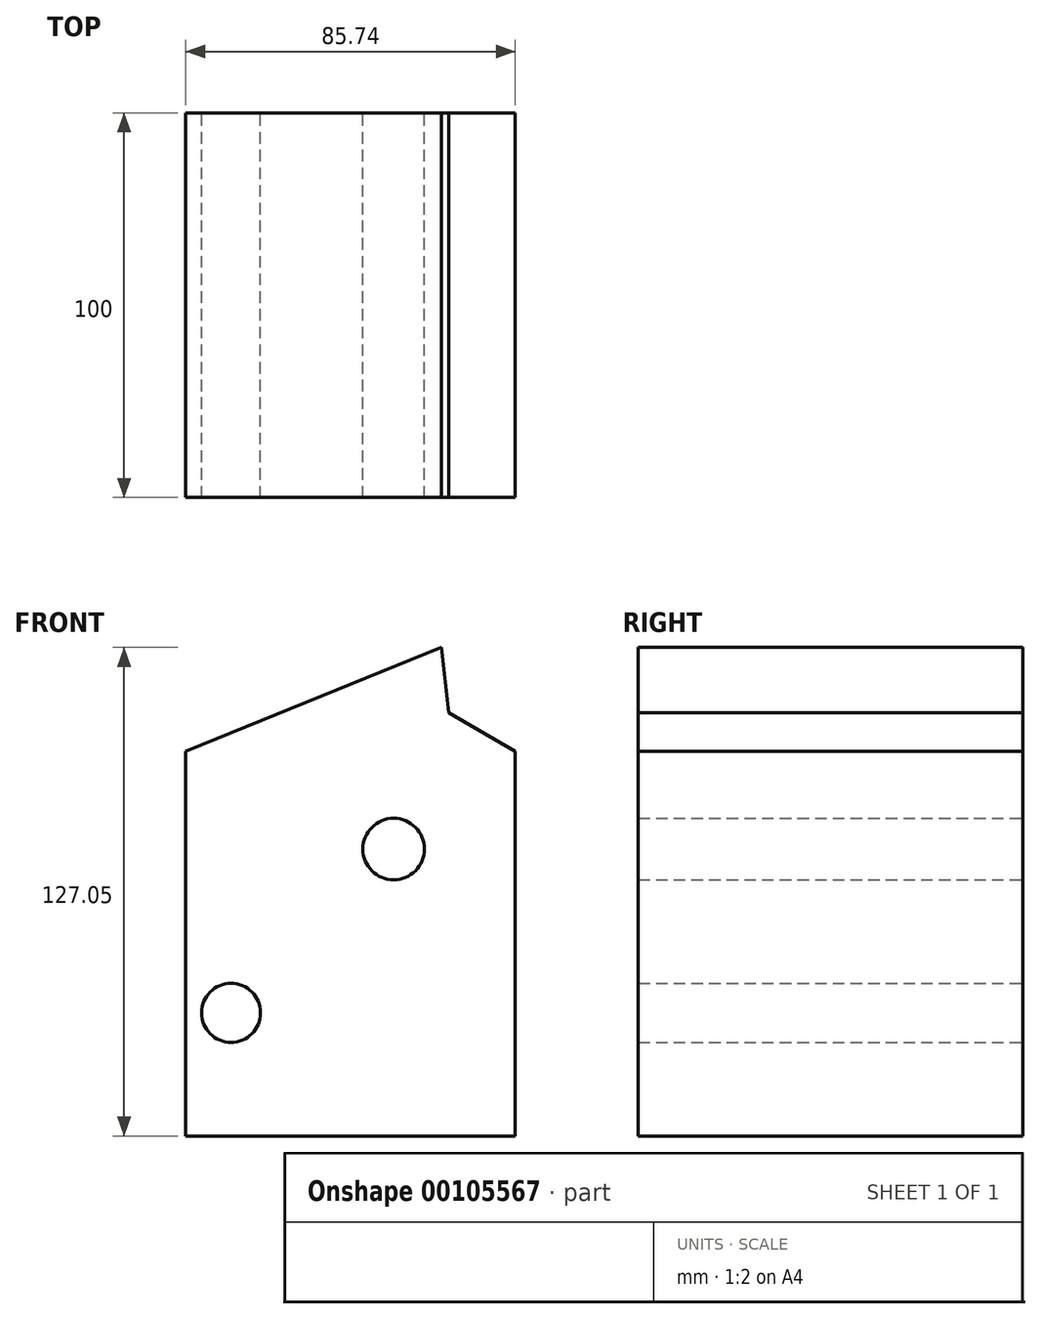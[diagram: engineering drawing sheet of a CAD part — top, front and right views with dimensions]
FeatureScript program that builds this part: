
annotation { "Feature Type Name" : "Feature", "Feature Type Description" : "" }
export const myFeature = defineFeature(function(context is Context, id is Id, definition is map)
    precondition{}
    {
        {
            var Q0;
            Q0=qCreatedBy(makeId("Front.planeOp"),FACE);
            var sketch = newSketch(context, id + "F0", { "sketchPlane" : qUnion([Q0])});
            skLineSegment(sketch, "E0.bottom", {"start": v(42.87, -50) * mm, "end": v(-42.87, -50) * mm});
            skLineSegment(sketch, "E0.top", {"start": v(42.87, 50) * mm, "end": v(-42.87, 50) * mm});
            skLineSegment(sketch, "E0.left", {"start": v(42.87, -50) * mm, "end": v(42.87, 50) * mm});
            skLineSegment(sketch, "E0.right", {"start": v(-42.87, -50) * mm, "end": v(-42.87, 50) * mm});
            skPoint(sketch, "E0.middle", {"position": v(0, 0) * mm});
            skLineSegment(sketch, "E1", {"start": v(-42.87, 50) * mm, "end": v(23.6, 77.05) * mm});
            skLineSegment(sketch, "E2", {"start": v(23.6, 77.05) * mm, "end": v(25.6, 60.07) * mm});
            skLineSegment(sketch, "E3", {"start": v(25.6, 60.07) * mm, "end": v(42.87, 50) * mm});
            skCircle(sketch, "E4", {"center": v(-31.08, -17.98) * mm, "radius": 7.66 * mm});
            skCircle(sketch, "E5", {"center": v(11.22, 24.6) * mm, "radius": 8 * mm});
            skSolve(sketch);
        }
        {
            var Q0;
            Q0 = qSketchRegion(id + "F0", true);
            extrude(context, id + "F1", {"entities" : qUnion([Q0]), "depth" : 100 * mm});
        }
    });
